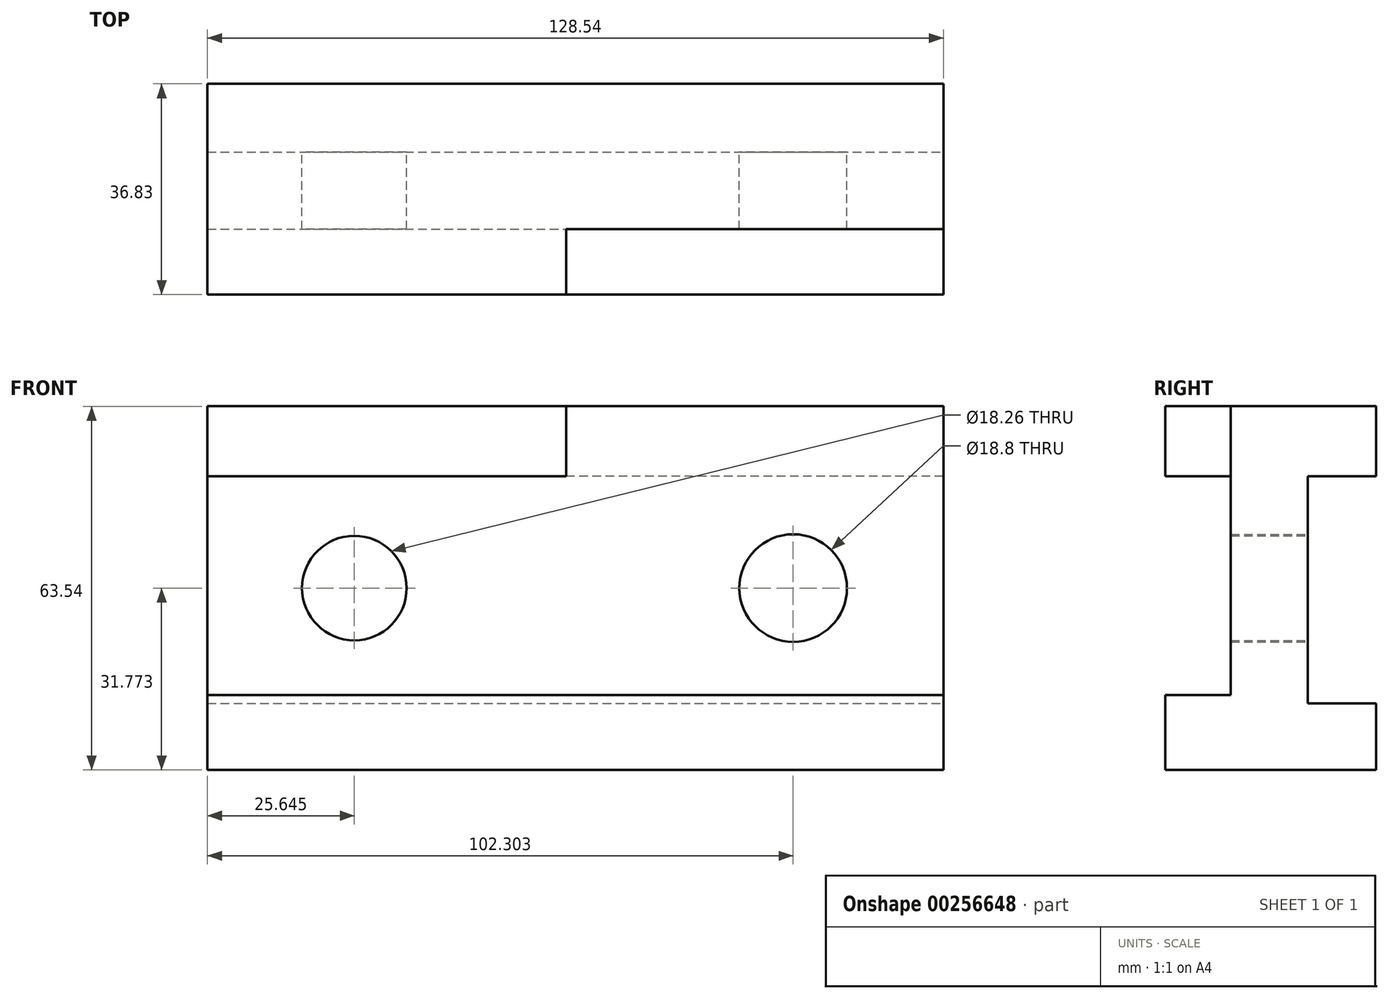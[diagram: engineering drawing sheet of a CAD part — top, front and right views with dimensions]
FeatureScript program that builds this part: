
annotation { "Feature Type Name" : "Feature", "Feature Type Description" : "" }
export const myFeature = defineFeature(function(context is Context, id is Id, definition is map)
    precondition{}
    {
        {
            var Q0;
            Q0=qCreatedBy(makeId("Front.planeOp"),FACE);
            var sketch = newSketch(context, id + "F0", { "sketchPlane" : qUnion([Q0])});
            skLineSegment(sketch, "E0.bottom", {"start": v(-66.16, 39.2) * mm, "end": v(62.38, 39.2) * mm});
            skLineSegment(sketch, "E0.top", {"start": v(-66.16, -24.34) * mm, "end": v(62.38, -24.34) * mm});
            skLineSegment(sketch, "E0.left", {"start": v(-66.16, 39.2) * mm, "end": v(-66.16, -24.34) * mm});
            skLineSegment(sketch, "E0.right", {"start": v(62.38, 39.2) * mm, "end": v(62.38, -24.34) * mm});
            skCircle(sketch, "E1", {"center": v(-40.52, 7.43) * mm, "radius": 9.13 * mm});
            skPoint(sketch, "E1.centerSnap0", {"position": v(-66.16, 7.43) * mm});
            skCircle(sketch, "E2", {"center": v(36.14, 7.43) * mm, "radius": 9.4 * mm});
            skPoint(sketch, "E2.centerSnap0", {"position": v(62.38, 7.43) * mm});
            skSolve(sketch);
        }
        {
            var Q0;
            Q0 = qSketchRegion(id + "F0", true);
            extrude(context, id + "F1", {"entities" : qUnion([Q0]), "depth" : 13.46 * mm});
        }
        {
            var Q0;
            Q0=makeQuery(id+"F1.opExtrude","CAP_FACE",FACE,{"disambiguationData":[OSD([sQuery(id+"F0.wireOp",EDGE,"E0.bottom"),sQuery(id+"F0.wireOp",EDGE,"E0.top"),sQuery(id+"F0.wireOp",EDGE,"E0.left"),sQuery(id+"F0.wireOp",EDGE,"E0.right"),sQuery(id+"F0.wireOp",EDGE,"E1"),sQuery(id+"F0.wireOp",EDGE,"E2")])],"isStart":false});
            var sketch = newSketch(context, id + "F2", { "sketchPlane" : qUnion([Q0])});
            skLineSegment(sketch, "E3.bottom", {"start": v(-66.16, 39.2) * mm, "end": v(-3.5, 39.2) * mm});
            skLineSegment(sketch, "E3.top", {"start": v(-66.16, 26.96) * mm, "end": v(-3.5, 26.96) * mm});
            skLineSegment(sketch, "E3.left", {"start": v(-66.16, 39.2) * mm, "end": v(-66.16, 26.96) * mm});
            skLineSegment(sketch, "E3.right", {"start": v(-3.5, 39.2) * mm, "end": v(-3.5, 26.96) * mm});
            skLineSegment(sketch, "E4.bottom", {"start": v(-66.16, -24.34) * mm, "end": v(62.38, -24.34) * mm});
            skLineSegment(sketch, "E4.top", {"start": v(-66.16, -11.22) * mm, "end": v(62.38, -11.22) * mm});
            skLineSegment(sketch, "E4.left", {"start": v(-66.16, -24.34) * mm, "end": v(-66.16, -11.22) * mm});
            skLineSegment(sketch, "E4.right", {"start": v(62.38, -24.34) * mm, "end": v(62.38, -11.22) * mm});
            skSolve(sketch);
        }
        {
            var Q0;
            Q0 = qSketchRegion(id + "F2", true);
            extrude(context, id + "F3", {"entities" : qUnion([Q0]), "operationType" : NewBodyOperationType.ADD, "depth" : 11.43 * mm});
        }
        {
            var Q0;
            Q0=makeQuery(id+"F1.opExtrude","CAP_FACE",FACE,{"disambiguationData":[OSD([sQuery(id+"F0.wireOp",EDGE,"E0.bottom"),sQuery(id+"F0.wireOp",EDGE,"E0.top"),sQuery(id+"F0.wireOp",EDGE,"E0.left"),sQuery(id+"F0.wireOp",EDGE,"E0.right"),sQuery(id+"F0.wireOp",EDGE,"E1"),sQuery(id+"F0.wireOp",EDGE,"E2")])],"isStart":true});
            var sketch = newSketch(context, id + "F4", { "sketchPlane" : qUnion([Q0])});
            skLineSegment(sketch, "E5.bottom", {"start": v(-62.38, 39.2) * mm, "end": v(66.16, 39.2) * mm});
            skLineSegment(sketch, "E5.top", {"start": v(-62.38, 26.96) * mm, "end": v(66.16, 26.96) * mm});
            skLineSegment(sketch, "E5.left", {"start": v(-62.38, 39.2) * mm, "end": v(-62.38, 26.96) * mm});
            skLineSegment(sketch, "E5.right", {"start": v(66.16, 39.2) * mm, "end": v(66.16, 26.96) * mm});
            skLineSegment(sketch, "E6.bottom", {"start": v(66.16, -24.34) * mm, "end": v(-62.38, -24.34) * mm});
            skLineSegment(sketch, "E6.top", {"start": v(66.16, -12.68) * mm, "end": v(-62.38, -12.68) * mm});
            skLineSegment(sketch, "E6.left", {"start": v(66.16, -24.34) * mm, "end": v(66.16, -12.68) * mm});
            skLineSegment(sketch, "E6.right", {"start": v(-62.38, -24.34) * mm, "end": v(-62.38, -12.68) * mm});
            skSolve(sketch);
        }
        {
            var Q0;
            Q0 = qSketchRegion(id + "F4", true);
            extrude(context, id + "F5", {"entities" : qUnion([Q0]), "operationType" : NewBodyOperationType.ADD, "depth" : 11.94 * mm});
        }
    });
